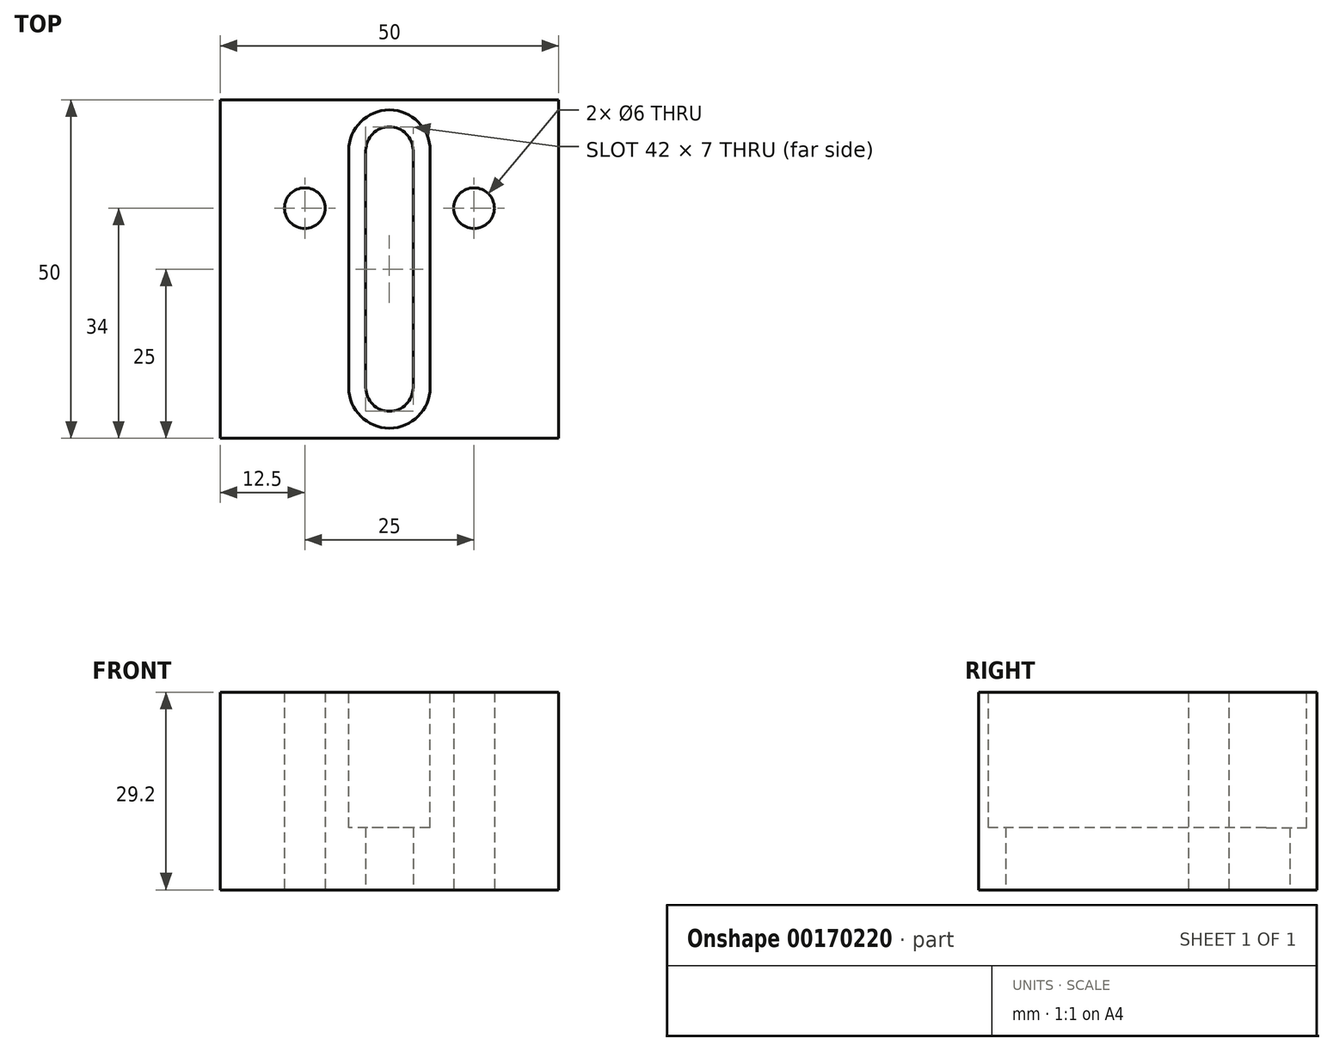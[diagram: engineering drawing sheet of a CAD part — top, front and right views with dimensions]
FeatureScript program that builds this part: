
annotation { "Feature Type Name" : "Feature", "Feature Type Description" : "" }
export const myFeature = defineFeature(function(context is Context, id is Id, definition is map)
    precondition{}
    {
        {
            var Q0;
            Q0=qCreatedBy(makeId("Top.planeOp"),FACE);
            var sketch = newSketch(context, id + "F0", { "sketchPlane" : qUnion([Q0])});
            skLineSegment(sketch, "E0.bottom", {"start": v(-25, 25) * mm, "end": v(25, 25) * mm});
            skLineSegment(sketch, "E0.top", {"start": v(-25, -25) * mm, "end": v(25, -25) * mm});
            skLineSegment(sketch, "E0.left", {"start": v(-25, 25) * mm, "end": v(-25, -25) * mm});
            skLineSegment(sketch, "E0.right", {"start": v(25, 25) * mm, "end": v(25, -25) * mm});
            skArc(sketch, "E1", {"start": v(3.5, 17.5) * mm, "mid": v(0, 21) * mm, "end": v(-3.5, 17.5) * mm});
            skArc(sketch, "E2", {"start": v(-3.5, -17.5) * mm, "mid": v(0, -21) * mm, "end": v(3.5, -17.5) * mm});
            skCircle(sketch, "E3", {"center": v(-12.5, 9) * mm, "radius": 3 * mm});
            skCircle(sketch, "E4", {"center": v(12.5, 9) * mm, "radius": 3 * mm});
            skLineSegment(sketch, "E5", {"start": v(-3.5, 17.5) * mm, "end": v(-3.5, -17.5) * mm});
            skLineSegment(sketch, "E6", {"start": v(3.5, 17.5) * mm, "end": v(3.5, -17.5) * mm});
            skSolve(sketch);
        }
        {
            var Q0;
            Q0 = qSketchRegion(id + "F0", true);
            extrude(context, id + "F1", {"entities" : qUnion([Q0]), "depth" : 29.2 * mm});
        }
        {
            var Q0;
            Q0=makeQuery(id+"F1.opExtrude","CAP_FACE",FACE,{"disambiguationData":[OSD([sQuery(id+"F0.wireOp",EDGE,"E0.bottom"),sQuery(id+"F0.wireOp",EDGE,"E0.top"),sQuery(id+"F0.wireOp",EDGE,"E0.left"),sQuery(id+"F0.wireOp",EDGE,"E0.right"),sQuery(id+"F0.wireOp",EDGE,"E1"),sQuery(id+"F0.wireOp",EDGE,"E2"),sQuery(id+"F0.wireOp",EDGE,"E3"),sQuery(id+"F0.wireOp",EDGE,"E4")])],"isStart":false});
            var sketch = newSketch(context, id + "F2", { "sketchPlane" : qUnion([Q0])});
            skArc(sketch, "E7", {"start": v(6, 17.5) * mm, "mid": v(0, 23.5) * mm, "end": v(-6, 17.5) * mm});
            skArc(sketch, "E8", {"start": v(-6, -17.5) * mm, "mid": v(0, -23.5) * mm, "end": v(6, -17.5) * mm});
            skLineSegment(sketch, "E9", {"start": v(-6, 17.5) * mm, "end": v(-6, -17.5) * mm});
            skLineSegment(sketch, "E10", {"start": v(6, -17.5) * mm, "end": v(6, 17.5) * mm});
            skSolve(sketch);
        }
        {
            var Q0;
            Q0 = qSketchRegion(id + "F2", true);
            extrude(context, id + "F3", {"entities" : qUnion([Q0]), "operationType" : NewBodyOperationType.REMOVE, "oppositeDirection" : true, "depth" : 20 * mm});
        }
    });
